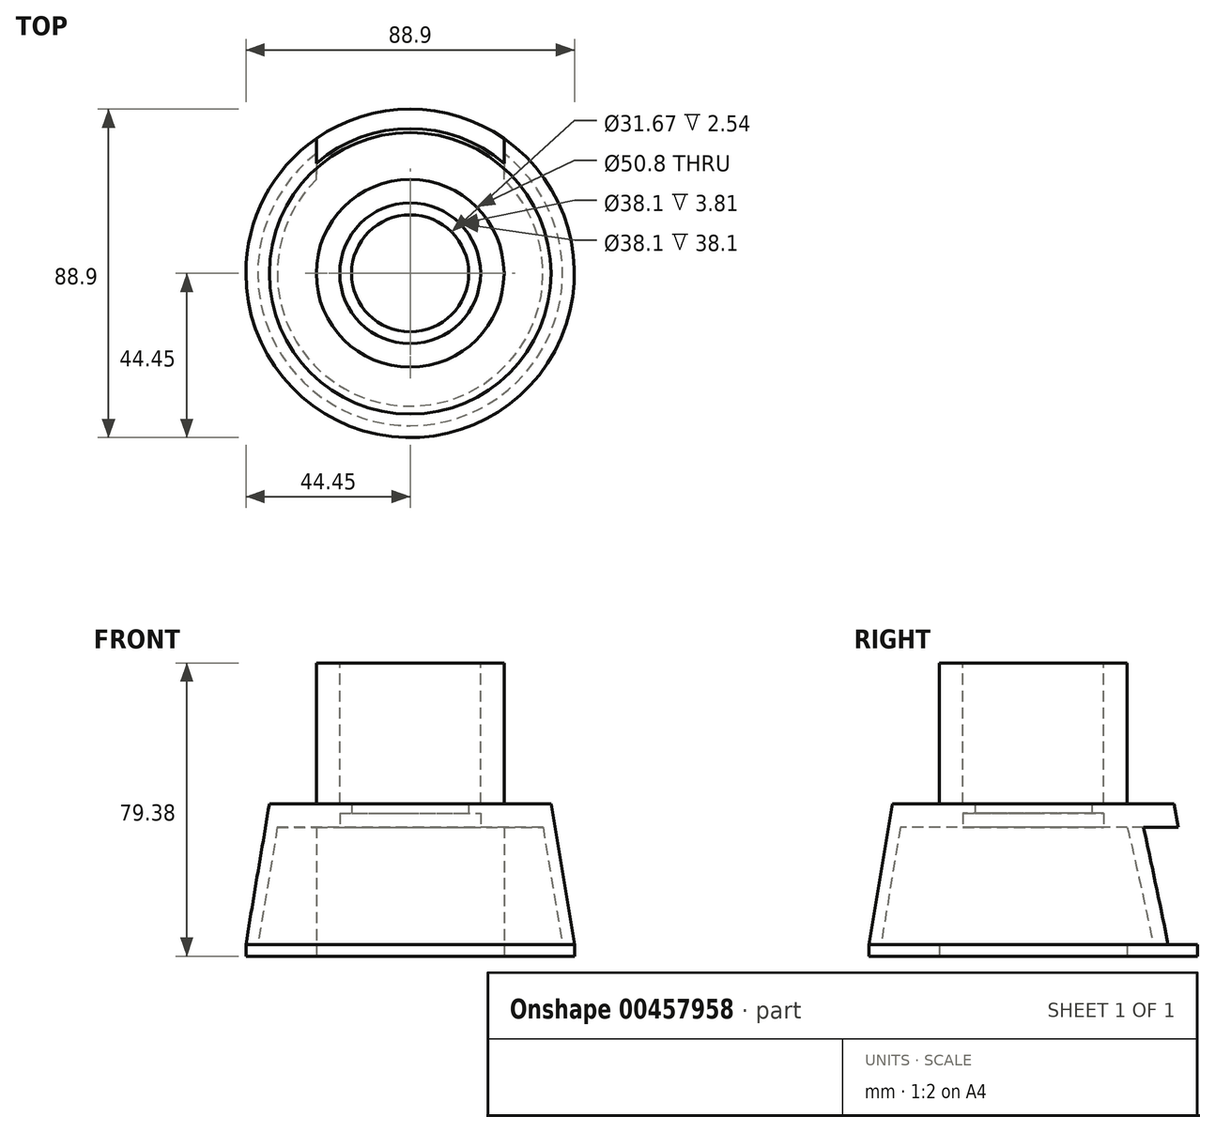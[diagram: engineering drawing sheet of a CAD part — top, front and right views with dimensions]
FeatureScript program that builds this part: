
annotation { "Feature Type Name" : "Feature", "Feature Type Description" : "" }
export const myFeature = defineFeature(function(context is Context, id is Id, definition is map)
    precondition{}
    {
        {
            var Q0;
            Q0=qCreatedBy(makeId("Front.planeOp"),FACE);
            var sketch = newSketch(context, id + "F0", { "sketchPlane" : qUnion([Q0])});
            skLineSegment(sketch, "E0", {"start": v(0, 0) * mm, "end": v(0, 385.96) * mm, "construction": true});
            skLineSegment(sketch, "E1", {"start": v(-44.45, 0) * mm, "end": v(-38.1, 38.1) * mm});
            skLineSegment(sketch, "E2", {"start": v(-38.1, 38.1) * mm, "end": v(-25.4, 38.1) * mm});
            skLineSegment(sketch, "E3", {"start": v(-25.4, 38.1) * mm, "end": v(-25.4, 76.2) * mm});
            skLineSegment(sketch, "E4", {"start": v(-25.4, 76.2) * mm, "end": v(-15.83, 76.2) * mm});
            skLineSegment(sketch, "E5", {"start": v(-35.94, 31.75) * mm, "end": v(-41.23, 0) * mm});
            skLineSegment(sketch, "E6", {"start": v(-44.45, -3.18) * mm, "end": v(-44.45, 0) * mm});
            skLineSegment(sketch, "E7", {"start": v(-41.23, 0) * mm, "end": v(-25.4, 0) * mm});
            skLineSegment(sketch, "E8", {"start": v(-25.4, 0) * mm, "end": v(-25.4, -3.18) * mm});
            skLineSegment(sketch, "E9", {"start": v(-25.4, -3.18) * mm, "end": v(-44.45, -3.18) * mm});
            skLineSegment(sketch, "E10", {"start": v(-15.83, 76.2) * mm, "end": v(-15.83, 35.56) * mm});
            skLineSegment(sketch, "E11", {"start": v(-15.83, 35.56) * mm, "end": v(-19.05, 35.56) * mm});
            skLineSegment(sketch, "E12", {"start": v(-35.94, 31.75) * mm, "end": v(-19.05, 31.75) * mm});
            skLineSegment(sketch, "E13", {"start": v(-19.05, 31.75) * mm, "end": v(-19.05, 35.56) * mm});
            skSolve(sketch);
        }
        {
            var Q0;
            Q0=qSketchRegion(id+"F0",true);
            var Q1;
            Q1=sQuery(id+"F0.wireOp",EDGE,"E0");
            revolve(context, id + "F1", {"entities" : qUnion([Q0]), "axis" : qUnion([Q1]), "revolveType" : RevolveType.FULL});
        }
        {
            var Q0;
            Q0=qCreatedBy(makeId("Front.planeOp"),FACE);
            var sketch = newSketch(context, id + "F2", { "sketchPlane" : qUnion([Q0])});
            skLineSegment(sketch, "E14.bottom", {"start": v(-25.4, 31.75) * mm, "end": v(25.4, 31.75) * mm});
            skLineSegment(sketch, "E14.top", {"start": v(-25.4, 0) * mm, "end": v(25.4, 0) * mm});
            skLineSegment(sketch, "E14.left", {"start": v(-25.4, 31.75) * mm, "end": v(-25.4, 0) * mm});
            skLineSegment(sketch, "E14.right", {"start": v(25.4, 31.75) * mm, "end": v(25.4, 0) * mm});
            skLineSegment(sketch, "E15.bottom", {"start": v(-25.4, 0) * mm, "end": v(-25.71, 5.44) * mm});
            skSolve(sketch);
        }
        {
            var Q0;
            Q0=qSketchRegion(id+"F2",true);
            extrude(context, id + "F3", {"entities" : qUnion([Q0]), "operationType" : NewBodyOperationType.REMOVE, "endBound" : BoundingType.THROUGH_ALL, "oppositeDirection" : true, "depth" : 25.4 * mm});
        }
        {
            var Q0;
            Q0=makeQuery(id+"F1.opRevolve","SWEPT_FACE",FACE,{"disambiguationData":[OSD([sQuery(id+"F0.wireOp",EDGE,"E4")])]});
            var sketch = newSketch(context, id + "F4", { "sketchPlane" : qUnion([Q0])});
            skCircle(sketch, "E16", {"center": v(0, 0) * mm, "radius": 19.05 * mm});
            skSolve(sketch);
        }
        {
            var Q0;
            Q0=qSketchRegion(id+"F4",true);
            extrude(context, id + "F5", {"entities" : qUnion([Q0]), "operationType" : NewBodyOperationType.REMOVE, "oppositeDirection" : true, "depth" : 38.1 * mm});
        }
    });
